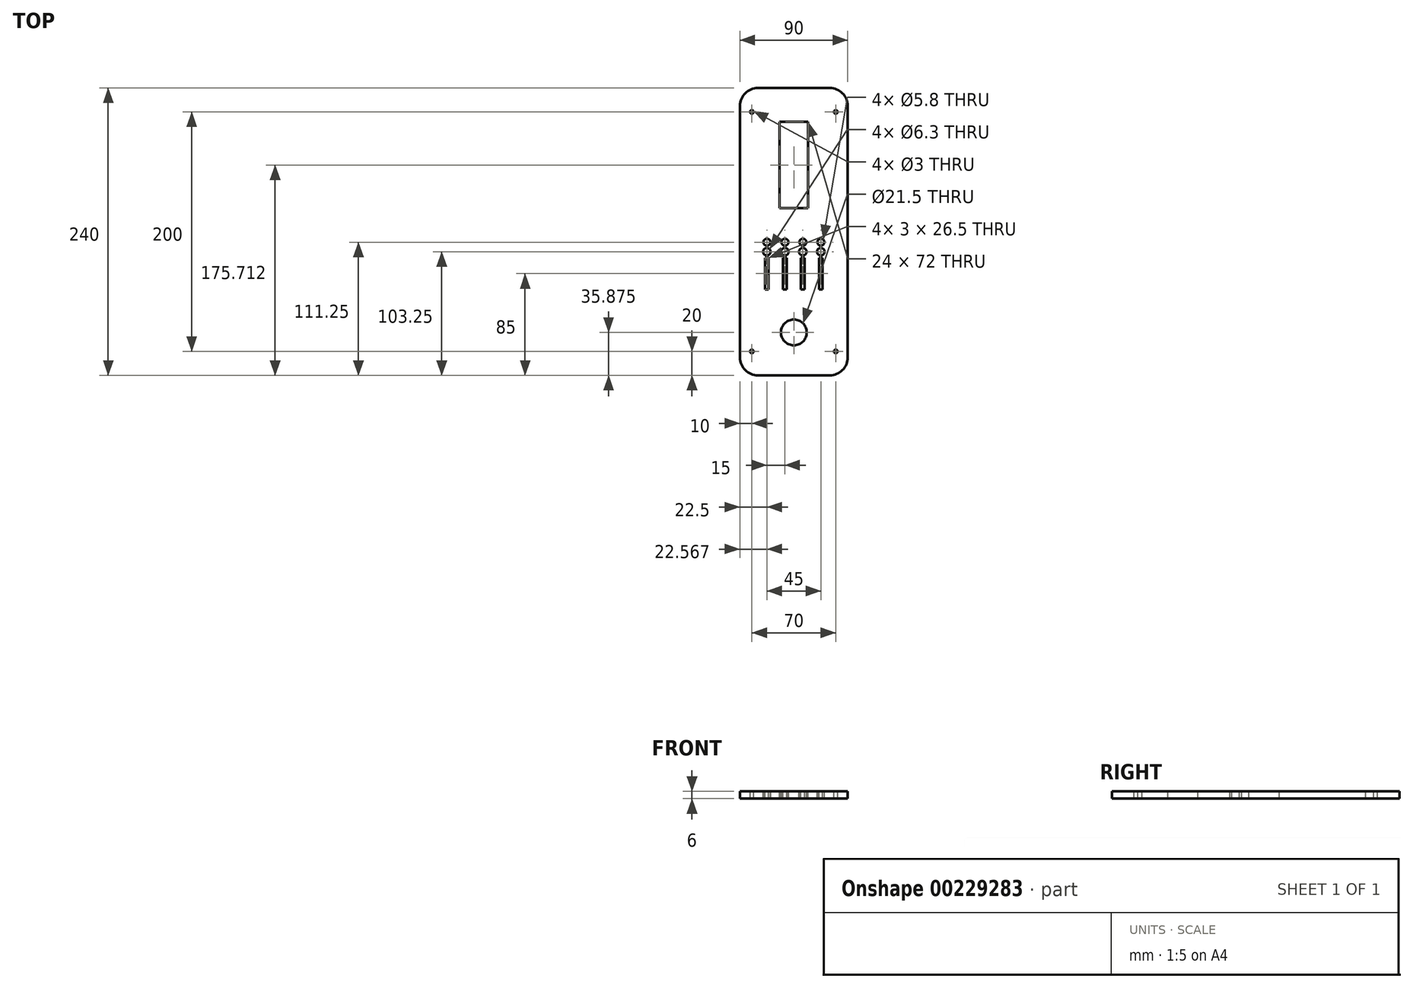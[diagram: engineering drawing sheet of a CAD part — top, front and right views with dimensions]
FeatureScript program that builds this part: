
annotation { "Feature Type Name" : "Feature", "Feature Type Description" : "" }
export const myFeature = defineFeature(function(context is Context, id is Id, definition is map)
    precondition{}
    {
        {
            var Q0;
            Q0=qCreatedBy(makeId("Top.planeOp"),FACE);
            var sketch = newSketch(context, id + "F0", { "sketchPlane" : qUnion([Q0])});
            skLineSegment(sketch, "E0.bottom", {"start": v(30, -120) * mm, "end": v(-30, -120) * mm});
            skLineSegment(sketch, "E0.top", {"start": v(30, 120) * mm, "end": v(-30, 120) * mm});
            skLineSegment(sketch, "E0.left", {"start": v(45, -105) * mm, "end": v(45, 105) * mm});
            skLineSegment(sketch, "E0.right", {"start": v(-45, -105) * mm, "end": v(-45, 105) * mm});
            skPoint(sketch, "E0.middle", {"position": v(0, 0) * mm});
            skPoint(sketch, "E1.visualSharp", {"position": v(-45, 120) * mm});
            skArc(sketch, "E1.filletArc", {"start": v(-30, 120) * mm, "mid": v(-40.6, 115.6) * mm, "end": v(-45, 105) * mm});
            skPoint(sketch, "E2.visualSharp", {"position": v(45, 120) * mm});
            skArc(sketch, "E2.filletArc", {"start": v(45, 105) * mm, "mid": v(40.6, 115.6) * mm, "end": v(30, 120) * mm});
            skPoint(sketch, "E3.visualSharp", {"position": v(-45, -120) * mm});
            skArc(sketch, "E3.filletArc", {"start": v(-45, -105) * mm, "mid": v(-40.6, -115.6) * mm, "end": v(-30, -120) * mm});
            skPoint(sketch, "E4.visualSharp", {"position": v(45, -120) * mm});
            skArc(sketch, "E4.filletArc", {"start": v(30, -120) * mm, "mid": v(40.6, -115.6) * mm, "end": v(45, -105) * mm});
            skSolve(sketch);
        }
        {
            var Q0;
            Q0=makeQuery(id+"F0.imprint","IMPRINT",FACE,{"disambiguationData":[TD([[makeQuery(id+"F0.imprint","IMPRINT",EDGE,{"derivedFrom":sQuery(id+"F0.wireOp",EDGE,"E0.bottom")}),-1.0]])]});
            extrude(context, id + "F1", {"entities" : qUnion([Q0]), "depth" : 6 * mm});
        }
        {
            var Q0;
            Q0=makeQuery(id+"F1.opExtrude","CAP_FACE",FACE,{"disambiguationData":[OSD([sQuery(id+"F0.wireOp",EDGE,"E0.bottom"),sQuery(id+"F0.wireOp",EDGE,"E0.top"),sQuery(id+"F0.wireOp",EDGE,"E0.left"),sQuery(id+"F0.wireOp",EDGE,"E0.right"),sQuery(id+"F0.wireOp",EDGE,"E1.filletArc"),sQuery(id+"F0.wireOp",EDGE,"E2.filletArc"),sQuery(id+"F0.wireOp",EDGE,"E3.filletArc"),sQuery(id+"F0.wireOp",EDGE,"E4.filletArc")])],"isStart":false});
            var sketch = newSketch(context, id + "F2", { "sketchPlane" : qUnion([Q0])});
            skLineSegment(sketch, "E5.bottom", {"start": v(12, 19.71) * mm, "end": v(-12, 19.71) * mm});
            skLineSegment(sketch, "E5.top", {"start": v(12, 91.71) * mm, "end": v(-12, 91.71) * mm});
            skLineSegment(sketch, "E5.left", {"start": v(12, 19.71) * mm, "end": v(12, 91.71) * mm});
            skLineSegment(sketch, "E5.right", {"start": v(-12, 19.71) * mm, "end": v(-12, 91.71) * mm});
            skPoint(sketch, "E5.middle", {"position": v(0, 55.71) * mm});
            skSolve(sketch);
        }
        {
            var Q0;
            Q0 = qSketchRegion(id + "F2", true);
            extrude(context, id + "F3", {"entities" : qUnion([Q0]), "operationType" : NewBodyOperationType.REMOVE, "endBound" : BoundingType.UP_TO_NEXT, "oppositeDirection" : true, "depth" : 25 * mm});
        }
        {
            var Q0;
            Q0=makeQuery(id+"F1.opExtrude","CAP_FACE",FACE,{"disambiguationData":[OSD([sQuery(id+"F0.wireOp",EDGE,"E0.bottom"),sQuery(id+"F0.wireOp",EDGE,"E0.top"),sQuery(id+"F0.wireOp",EDGE,"E0.left"),sQuery(id+"F0.wireOp",EDGE,"E0.right"),sQuery(id+"F0.wireOp",EDGE,"E1.filletArc"),sQuery(id+"F0.wireOp",EDGE,"E2.filletArc"),sQuery(id+"F0.wireOp",EDGE,"E3.filletArc"),sQuery(id+"F0.wireOp",EDGE,"E4.filletArc")])],"isStart":false});
            var sketch = newSketch(context, id + "F4", { "sketchPlane" : qUnion([Q0])});
            skLineSegment(sketch, "E6.bottom", {"start": v(-21, -48.25) * mm, "end": v(-24, -48.25) * mm});
            skLineSegment(sketch, "E6.top", {"start": v(-21, -21.75) * mm, "end": v(-24, -21.75) * mm});
            skLineSegment(sketch, "E6.left", {"start": v(-21, -48.25) * mm, "end": v(-21, -21.75) * mm});
            skLineSegment(sketch, "E6.right", {"start": v(-24, -48.25) * mm, "end": v(-24, -21.75) * mm});
            skPoint(sketch, "E6.middle", {"position": v(-22.5, -35) * mm});
            skCircle(sketch, "E7", {"center": v(-22.43, -8.75) * mm, "radius": 2.9 * mm});
            skCircle(sketch, "E8", {"center": v(-22.5, -16.75) * mm, "radius": 3.15 * mm});
            skLineSegment(sketch, "E9", {"start": v(-22.5, -35) * mm, "end": v(-22.5, -21.75) * mm, "construction": true});
            skLineSegment(sketch, "E10", {"start": v(-22.5, -21.75) * mm, "end": v(-22.5, -16.75) * mm, "construction": true});
            skLineSegment(sketch, "E11", {"start": v(-22.43, -8.75) * mm, "end": v(-22.5, -16.75) * mm, "construction": true});
            skPoint(sketch, "E12.1.0.0", {"position": v(-7.5, -35) * mm});
            skCircle(sketch, "E12.1.0.1", {"center": v(-7.5, -16.75) * mm, "radius": 3.15 * mm});
            skLineSegment(sketch, "E12.1.0.2", {"start": v(-6, -48.25) * mm, "end": v(-9, -48.25) * mm});
            skLineSegment(sketch, "E12.1.0.3", {"start": v(-6, -48.25) * mm, "end": v(-6, -21.75) * mm});
            skLineSegment(sketch, "E12.1.0.4", {"start": v(-7.5, -21.75) * mm, "end": v(-7.5, -16.75) * mm, "construction": true});
            skCircle(sketch, "E12.1.0.5", {"center": v(-7.43, -8.75) * mm, "radius": 2.9 * mm});
            skLineSegment(sketch, "E12.1.0.6", {"start": v(-9, -48.25) * mm, "end": v(-9, -21.75) * mm});
            skLineSegment(sketch, "E12.1.0.7", {"start": v(-7.43, -8.75) * mm, "end": v(-7.5, -16.75) * mm, "construction": true});
            skLineSegment(sketch, "E12.1.0.8", {"start": v(-7.5, -35) * mm, "end": v(-7.5, -21.75) * mm, "construction": true});
            skLineSegment(sketch, "E12.1.0.9", {"start": v(-6, -21.75) * mm, "end": v(-9, -21.75) * mm});
            skPoint(sketch, "E12.2.0.0", {"position": v(7.5, -35) * mm});
            skCircle(sketch, "E12.2.0.1", {"center": v(7.5, -16.75) * mm, "radius": 3.15 * mm});
            skLineSegment(sketch, "E12.2.0.2", {"start": v(9, -48.25) * mm, "end": v(6, -48.25) * mm});
            skLineSegment(sketch, "E12.2.0.3", {"start": v(9, -48.25) * mm, "end": v(9, -21.75) * mm});
            skLineSegment(sketch, "E12.2.0.4", {"start": v(7.5, -21.75) * mm, "end": v(7.5, -16.75) * mm, "construction": true});
            skCircle(sketch, "E12.2.0.5", {"center": v(7.57, -8.75) * mm, "radius": 2.9 * mm});
            skLineSegment(sketch, "E12.2.0.6", {"start": v(6, -48.25) * mm, "end": v(6, -21.75) * mm});
            skLineSegment(sketch, "E12.2.0.7", {"start": v(7.57, -8.75) * mm, "end": v(7.5, -16.75) * mm, "construction": true});
            skLineSegment(sketch, "E12.2.0.8", {"start": v(7.5, -35) * mm, "end": v(7.5, -21.75) * mm, "construction": true});
            skLineSegment(sketch, "E12.2.0.9", {"start": v(9, -21.75) * mm, "end": v(6, -21.75) * mm});
            skPoint(sketch, "E12.3.0.0", {"position": v(22.5, -35) * mm});
            skCircle(sketch, "E12.3.0.1", {"center": v(22.5, -16.75) * mm, "radius": 3.15 * mm});
            skLineSegment(sketch, "E12.3.0.2", {"start": v(24, -48.25) * mm, "end": v(21, -48.25) * mm});
            skLineSegment(sketch, "E12.3.0.3", {"start": v(24, -48.25) * mm, "end": v(24, -21.75) * mm});
            skLineSegment(sketch, "E12.3.0.4", {"start": v(22.5, -21.75) * mm, "end": v(22.5, -16.75) * mm, "construction": true});
            skCircle(sketch, "E12.3.0.5", {"center": v(22.57, -8.75) * mm, "radius": 2.9 * mm});
            skLineSegment(sketch, "E12.3.0.6", {"start": v(21, -48.25) * mm, "end": v(21, -21.75) * mm});
            skLineSegment(sketch, "E12.3.0.7", {"start": v(22.57, -8.75) * mm, "end": v(22.5, -16.75) * mm, "construction": true});
            skLineSegment(sketch, "E12.3.0.8", {"start": v(22.5, -35) * mm, "end": v(22.5, -21.75) * mm, "construction": true});
            skLineSegment(sketch, "E12.3.0.9", {"start": v(24, -21.75) * mm, "end": v(21, -21.75) * mm});
            skLineSegment(sketch, "E12.direction1", {"start": v(-24, -48.25) * mm, "end": v(-9, -48.25) * mm, "construction": true});
            skSolve(sketch);
        }
        {
            var Q0;
            Q0 = qSketchRegion(id + "F4", true);
            extrude(context, id + "F5", {"entities" : qUnion([Q0]), "operationType" : NewBodyOperationType.REMOVE, "endBound" : BoundingType.UP_TO_NEXT, "oppositeDirection" : true, "depth" : 25 * mm});
        }
        {
            var Q0;
            Q0=makeQuery(id+"F1.opExtrude","CAP_FACE",FACE,{"disambiguationData":[OSD([sQuery(id+"F0.wireOp",EDGE,"E0.bottom"),sQuery(id+"F0.wireOp",EDGE,"E0.top"),sQuery(id+"F0.wireOp",EDGE,"E0.left"),sQuery(id+"F0.wireOp",EDGE,"E0.right"),sQuery(id+"F0.wireOp",EDGE,"E1.filletArc"),sQuery(id+"F0.wireOp",EDGE,"E2.filletArc"),sQuery(id+"F0.wireOp",EDGE,"E3.filletArc"),sQuery(id+"F0.wireOp",EDGE,"E4.filletArc")])],"isStart":false});
            var sketch = newSketch(context, id + "F6", { "sketchPlane" : qUnion([Q0])});
            skCircle(sketch, "E13", {"center": v(0, -84.12) * mm, "radius": 10.75 * mm});
            skLineSegment(sketch, "E14", {"start": v(-6, -48.25) * mm, "end": v(6, -48.25) * mm, "construction": true});
            skLineSegment(sketch, "E15", {"start": v(0, -48.25) * mm, "end": v(0, -84.12) * mm, "construction": true});
            skLineSegment(sketch, "E16", {"start": v(0, -120) * mm, "end": v(0, -84.12) * mm, "construction": true});
            skSolve(sketch);
        }
        {
            var Q0;
            Q0 = qSketchRegion(id + "F6", true);
            extrude(context, id + "F7", {"entities" : qUnion([Q0]), "operationType" : NewBodyOperationType.REMOVE, "endBound" : BoundingType.UP_TO_NEXT, "oppositeDirection" : true, "depth" : 25 * mm});
        }
        {
            var Q0;
            Q0=makeQuery(id+"F1.opExtrude","CAP_FACE",FACE,{"disambiguationData":[OSD([sQuery(id+"F0.wireOp",EDGE,"E0.bottom"),sQuery(id+"F0.wireOp",EDGE,"E0.top"),sQuery(id+"F0.wireOp",EDGE,"E0.left"),sQuery(id+"F0.wireOp",EDGE,"E0.right"),sQuery(id+"F0.wireOp",EDGE,"E1.filletArc"),sQuery(id+"F0.wireOp",EDGE,"E2.filletArc"),sQuery(id+"F0.wireOp",EDGE,"E3.filletArc"),sQuery(id+"F0.wireOp",EDGE,"E4.filletArc")])],"isStart":false});
            var sketch = newSketch(context, id + "F8", { "sketchPlane" : qUnion([Q0])});
            skLineSegment(sketch, "E17.bottom", {"start": v(35, -100) * mm, "end": v(-35, -100) * mm, "construction": true});
            skLineSegment(sketch, "E17.top", {"start": v(35, 100) * mm, "end": v(-35, 100) * mm, "construction": true});
            skLineSegment(sketch, "E17.left", {"start": v(35, -100) * mm, "end": v(35, 100) * mm, "construction": true});
            skLineSegment(sketch, "E17.right", {"start": v(-35, -100) * mm, "end": v(-35, 100) * mm, "construction": true});
            skPoint(sketch, "E17.middle", {"position": v(0, 0) * mm});
            skCircle(sketch, "E18", {"center": v(-35, -100) * mm, "radius": 1.5 * mm});
            skCircle(sketch, "E19", {"center": v(35, -100) * mm, "radius": 1.5 * mm});
            skCircle(sketch, "E20", {"center": v(35, 100) * mm, "radius": 1.5 * mm});
            skCircle(sketch, "E21", {"center": v(-35, 100) * mm, "radius": 1.5 * mm});
            skSolve(sketch);
        }
        {
            var Q0;
            Q0 = qSketchRegion(id + "F8", true);
            extrude(context, id + "F9", {"entities" : qUnion([Q0]), "operationType" : NewBodyOperationType.REMOVE, "endBound" : BoundingType.UP_TO_NEXT, "oppositeDirection" : true, "depth" : 25 * mm});
        }
    });
